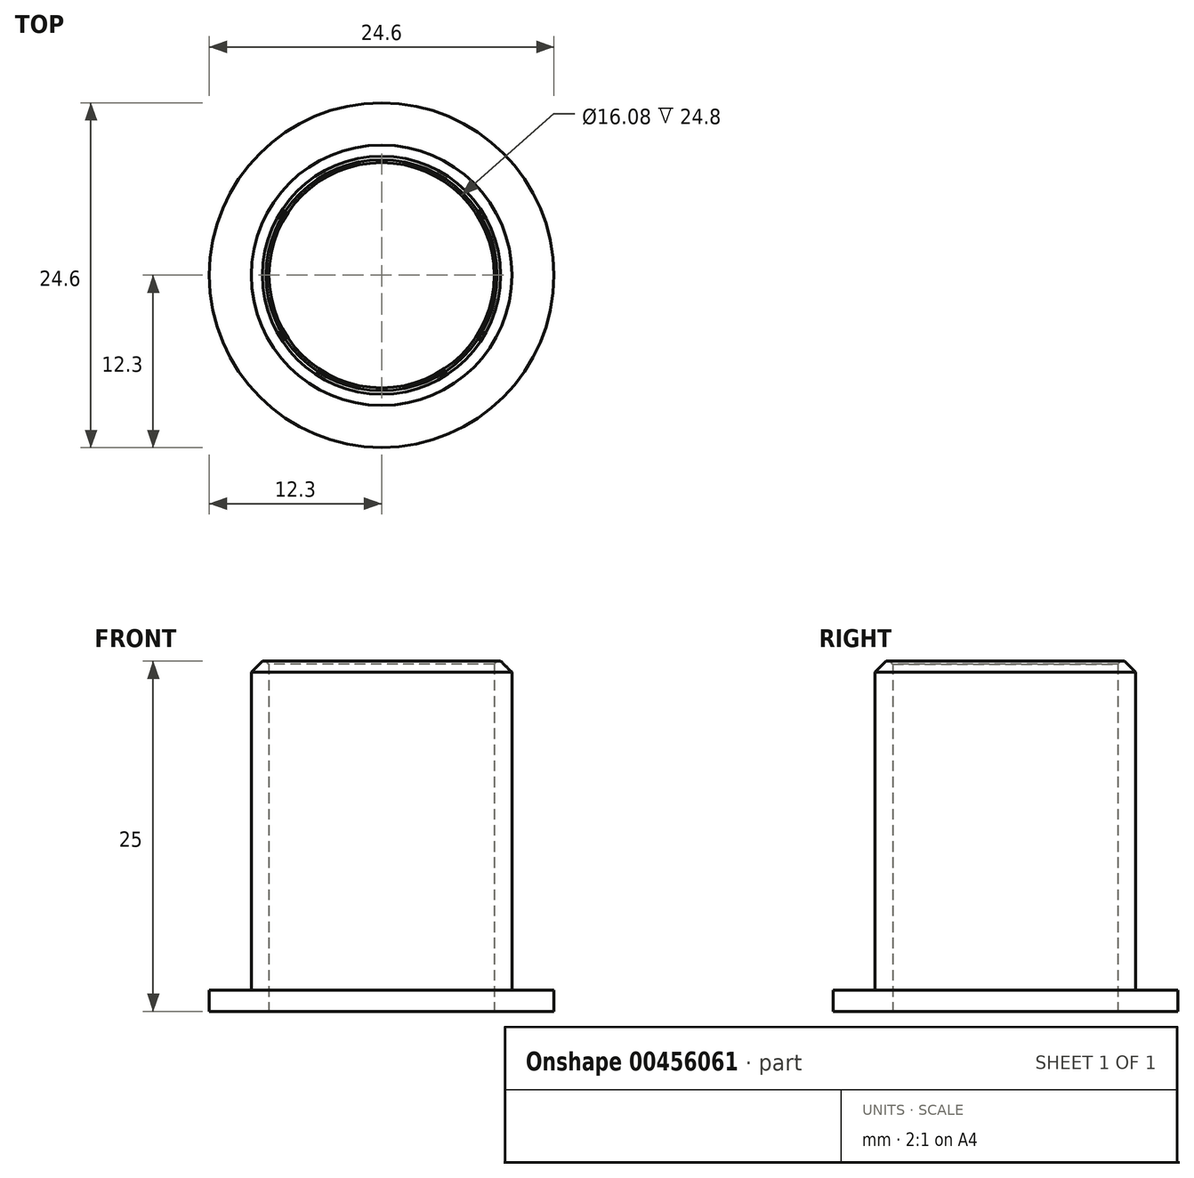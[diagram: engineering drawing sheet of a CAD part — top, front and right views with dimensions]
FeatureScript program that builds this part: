
annotation { "Feature Type Name" : "Feature", "Feature Type Description" : "" }
export const myFeature = defineFeature(function(context is Context, id is Id, definition is map)
    precondition{}
    {
        {
            var Q0;
            Q0=qCreatedBy(makeId("Top.planeOp"),FACE);
            var sketch = newSketch(context, id + "F0", { "sketchPlane" : qUnion([Q0])});
            skCircle(sketch, "E0", {"center": v(0, 0) * mm, "radius": 12.3 * mm});
            skCircle(sketch, "E1", {"center": v(0, 0) * mm, "radius": 9.3 * mm});
            skCircle(sketch, "E2", {"center": v(0, 0) * mm, "radius": 8.04 * mm});
            skSolve(sketch);
        }
        {
            var Q0;
            Q0=makeQuery(id+"F0.imprint","IMPRINT",FACE,{"disambiguationData":[TD([[makeQuery(id+"F0.imprint","IMPRINT",EDGE,{"derivedFrom":sQuery(id+"F0.wireOp",EDGE,"E0")}),1.0]])]});
            extrude(context, id + "F1", {"entities" : qUnion([Q0]), "depth" : 1.5 * mm});
        }
        {
            var Q0;
            Q0=makeQuery(id+"F0.imprint","IMPRINT",FACE,{"disambiguationData":[TD([[makeQuery(id+"F0.imprint","IMPRINT",EDGE,{"derivedFrom":sQuery(id+"F0.wireOp",EDGE,"E1")}),1.0]])]});
            extrude(context, id + "F2", {"entities" : qUnion([Q0]), "operationType" : NewBodyOperationType.ADD, "depth" : 25 * mm});
        }
        {
            var Q0;
            Q0=makeQuery(id+"F2.opExtrude","CAP_EDGE",EDGE,{"disambiguationData":[OSD([sQuery(id+"F0.wireOp",EDGE,"E1")])],"isStart":false});
            chamfer(context, id + "F3", {"entities" : qUnion([Q0]), "width" : 0.8 * mm, "tangentPropagation" : true});
        }
        {
            var Q0;
            Q0=makeQuery(id+"F2.opExtrude","CAP_EDGE",EDGE,{"disambiguationData":[OSD([sQuery(id+"F0.wireOp",EDGE,"E2")])],"isStart":false});
            chamfer(context, id + "F4", {"entities" : qUnion([Q0]), "width" : 0.2 * mm, "tangentPropagation" : true});
        }
    });
